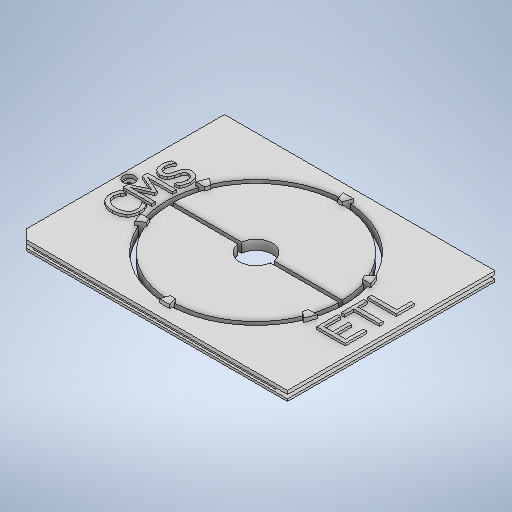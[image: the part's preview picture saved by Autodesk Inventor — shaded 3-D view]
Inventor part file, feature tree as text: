
AUTODESK INVENTOR PART (.ipt)
format: ipt  version: 2025 (Build 290162000, 162)  size: 537,600 bytes
history: native  units: mm
features: sketch x14, extrude x13, emboss x1
ambient origin geometry x8: Origin, YZ Plane, XZ Plane, XY Plane, X Axis, Y Axis, Z Axis, Center Point
bodies: Solid1 (feature_tree)
feature tree (28):
  extrude  "Extrusion1"  Depth=57.5mm
  extrude  "Extrusion2"  TaperAngle=45.0deg  [1 undecoded]
  extrude  "Extrusion3"  TaperAngle=0.0deg  [1 undecoded]
  extrude  "Extrusion4"  Depth=0.5mm
  extrude  "Extrusion5"  Depth=0.5mm
  extrude  "Extrusion6"  Depth=0.8mm TaperAngle=0.0deg
  sketch  "Sketch7"  dims[d20=38.0mm d21=40.0mm]
  extrude  "Extrusion7"  TaperAngle=0.0deg  [1 undecoded]
  extrude  "Extrusion8"  Depth=40.0mm
  extrude  "Extrusion9"  TaperAngle=0.0deg  [1 undecoded]
  extrude  "Extrusion10"  Depth=10.0mm TaperAngle=0.0deg
  extrude  "Extrusion11"  Depth=0.75mm
  extrude  "Extrusion12"  Depth=10.0mm
  emboss  "Emboss1"
  extrude  "Extrusion13"  Depth=19.198622mm
  sketch  "Sketch1"  dims[d0=44.1mm d1=57.5mm]
  sketch  "Sketch2"  dims[d5=2.0mm d6=0.0mm d7=0.0mm]
  sketch  "Sketch3"  dims[d8=0.5mm d9=3.0mm]
  sketch  "Sketch4"  dims[d10=0.8mm d11=0.0mm d12=0.5mm]
  sketch  "Sketch5"  dims[d13=0.5mm d14=0.8mm d15=0.0mm]
  sketch  "Sketch6"  dims[d16=0.75mm d17=0.0mm d18=0.0mm d19=0.0mm]
  sketch  "Sketch8"  dims[d22=10.0mm d23=0.0mm d24=0.0mm d25=0.0mm]
  sketch  "Sketch9"  dims[d26=1.0mm d27=10.0mm d28=0.0mm]
  sketch  "Sketch10"  dims[d29=0.75mm d30=36.5mm]
  sketch  "Sketch Circular Pattern1"  dims[d2=0.5mm d3=0.0mm d4=45.0deg]
  sketch  "Sketch11"  dims[d31=10.0mm d32=0.0mm d33=1.0mm]
  sketch  "Sketch12"  dims[d34=2.25mm d35=19.198622mm]
  sketch  "Sketch13"  dims[d36=19.198622mm d37=19.198622mm d39=30.0mm d41=24.260077mm d43=0.75mm d44=2.05mm d45=0.0mm d46=0.0mm d47=0.0mm d48=0.0mm d50=0.5mm d51=0.0mm d52=2.5mm d53=0.0mm d54=0.0mm]
note: 4 required parameter values undecoded (feature->parameter linkage not recoverable at this tier; creation-order binding heuristic only, values carry confidence <= 0.55)
